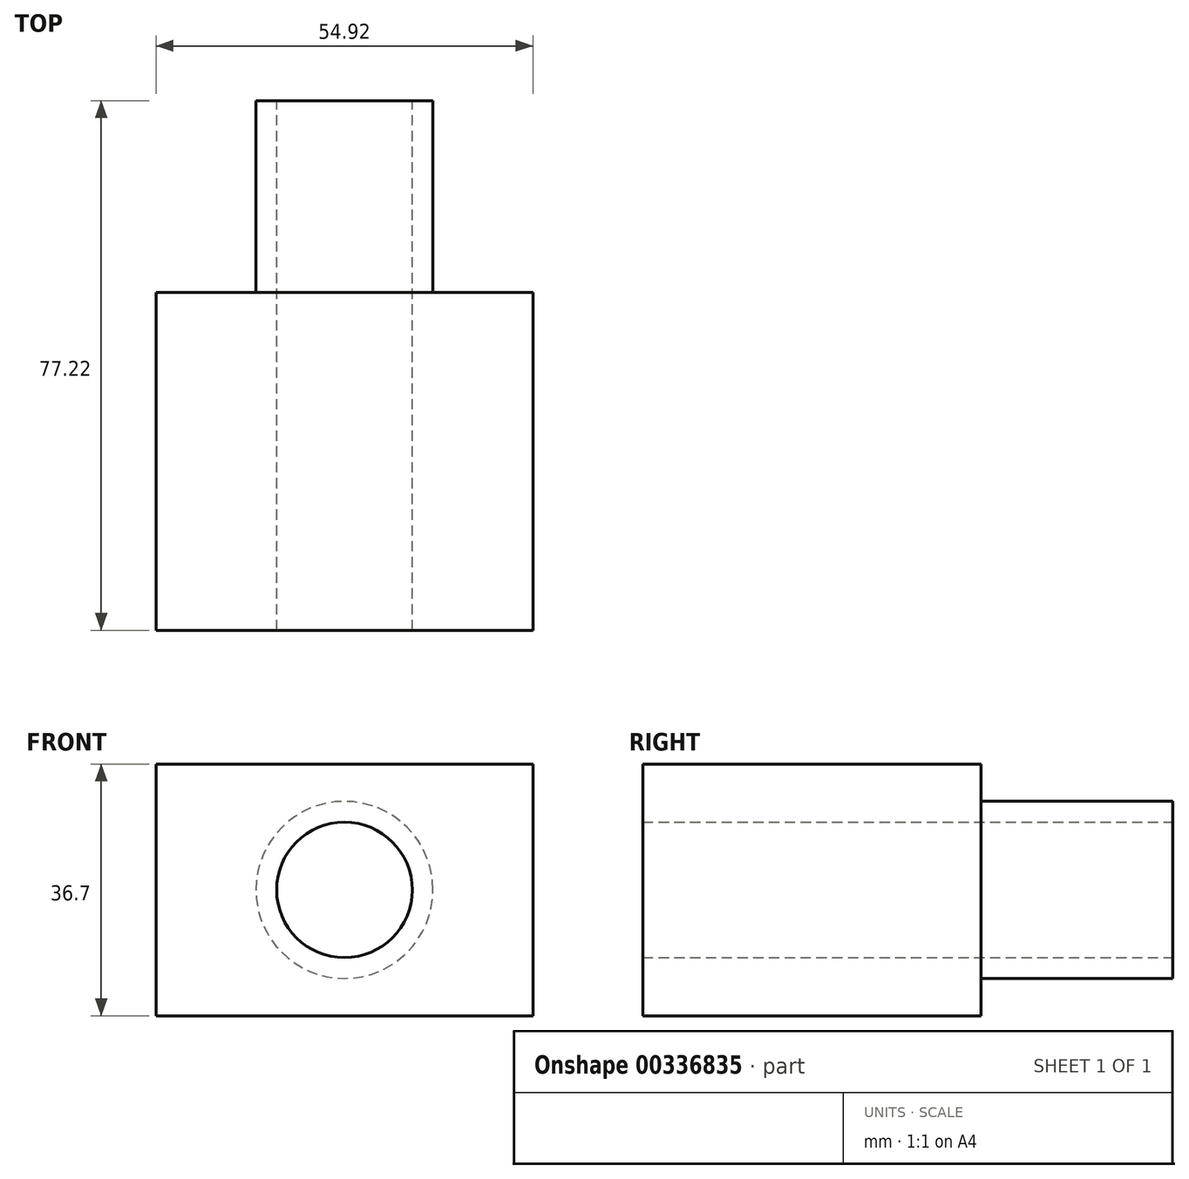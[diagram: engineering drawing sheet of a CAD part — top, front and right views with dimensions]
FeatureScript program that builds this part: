
annotation { "Feature Type Name" : "Feature", "Feature Type Description" : "" }
export const myFeature = defineFeature(function(context is Context, id is Id, definition is map)
    precondition{}
    {
        {
            var Q0;
            Q0=qCreatedBy(makeId("Front.planeOp"),FACE);
            var sketch = newSketch(context, id + "F0", { "sketchPlane" : qUnion([Q0])});
            skLineSegment(sketch, "E0.bottom", {"start": v(27.46, 18.35) * mm, "end": v(-27.46, 18.35) * mm});
            skLineSegment(sketch, "E0.top", {"start": v(27.46, -18.35) * mm, "end": v(-27.46, -18.35) * mm});
            skLineSegment(sketch, "E0.left", {"start": v(27.46, 18.35) * mm, "end": v(27.46, -18.35) * mm});
            skLineSegment(sketch, "E0.right", {"start": v(-27.46, 18.35) * mm, "end": v(-27.46, -18.35) * mm});
            skPoint(sketch, "E0.middle", {"position": v(0, 0) * mm});
            skSolve(sketch);
        }
        {
            var Q0;
            Q0=makeQuery(id+"F0.imprint","IMPRINT",FACE,{"disambiguationData":[TD([[makeQuery(id+"F0.imprint","IMPRINT",EDGE,{"derivedFrom":sQuery(id+"F0.wireOp",EDGE,"E0.bottom")}),1.0]])]});
            extrude(context, id + "F1", {"entities" : qUnion([Q0]), "depth" : 49.28 * mm});
        }
        {
            var Q0;
            Q0=qCreatedBy(makeId("Front.planeOp"),FACE);
            var sketch = newSketch(context, id + "F2", { "sketchPlane" : qUnion([Q0])});
            skCircle(sketch, "E1", {"center": v(0, 0) * mm, "radius": 12.9 * mm});
            skSolve(sketch);
        }
        {
            var Q0;
            Q0=makeQuery(id+"F2.imprint","IMPRINT",FACE,{"disambiguationData":[TD([[makeQuery(id+"F2.imprint","IMPRINT",EDGE,{"derivedFrom":sQuery(id+"F2.wireOp",EDGE,"E1")}),1.0]])]});
            extrude(context, id + "F3", {"entities" : qUnion([Q0]), "operationType" : NewBodyOperationType.ADD, "oppositeDirection" : true, "depth" : 27.94 * mm});
        }
        {
            var Q0;
            Q0=makeQuery(id+"F3.opExtrude","CAP_FACE",FACE,{"disambiguationData":[OSD([sQuery(id+"F2.wireOp",EDGE,"E1")])],"isStart":false});
            var sketch = newSketch(context, id + "F4", { "sketchPlane" : qUnion([Q0])});
            skCircle(sketch, "E2", {"center": v(0, 0) * mm, "radius": 9.88 * mm});
            skSolve(sketch);
        }
        {
            var Q0;
            Q0=makeQuery(id+"F4.imprint","IMPRINT",FACE,{"disambiguationData":[TD([[makeQuery(id+"F4.imprint","IMPRINT",EDGE,{"derivedFrom":sQuery(id+"F4.wireOp",EDGE,"E2")}),1.0]])]});
            extrude(context, id + "F5", {"entities" : qUnion([Q0]), "operationType" : NewBodyOperationType.REMOVE, "oppositeDirection" : true, "depth" : 92.2 * mm});
        }
    });
